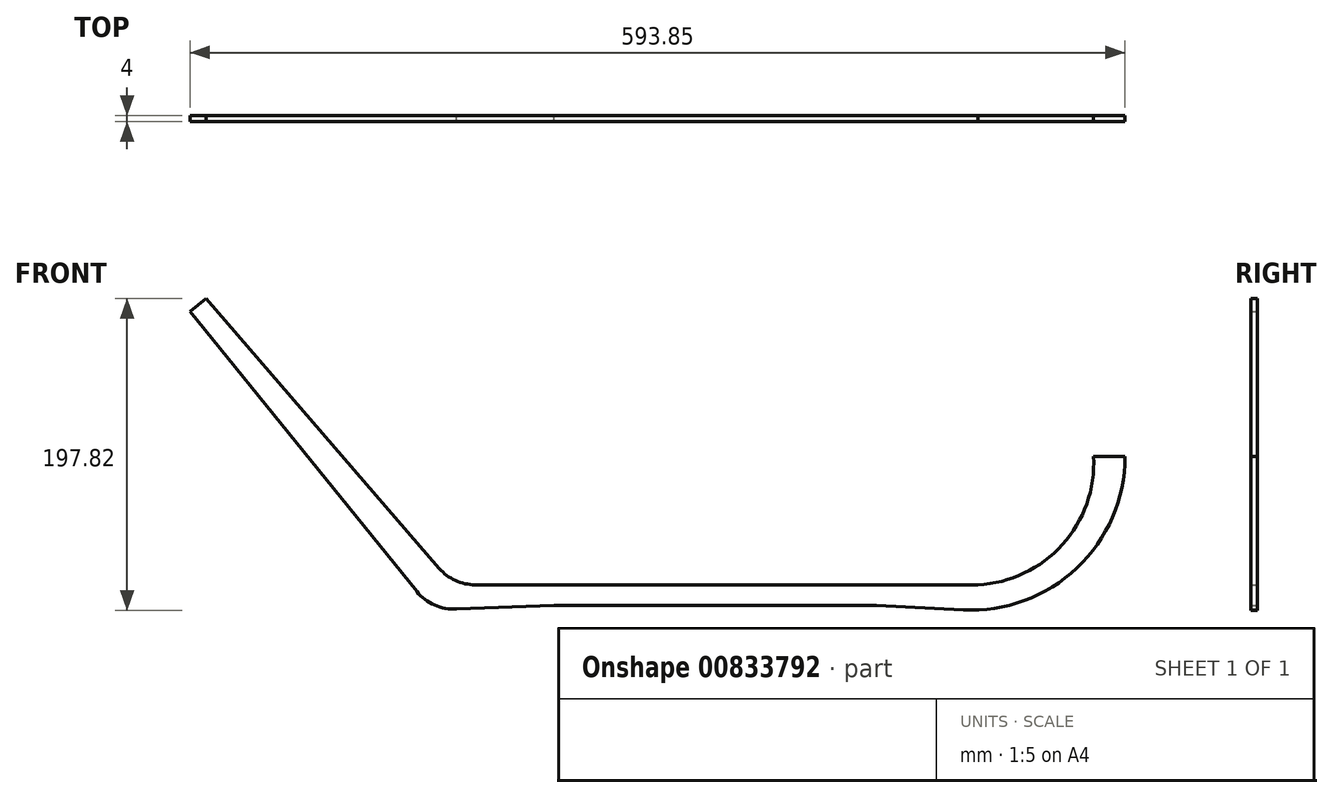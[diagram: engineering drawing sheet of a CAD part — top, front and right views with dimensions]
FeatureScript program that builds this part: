
annotation { "Feature Type Name" : "Feature", "Feature Type Description" : "" }
export const myFeature = defineFeature(function(context is Context, id is Id, definition is map)
    precondition{}
    {
        {
            var Q0;
            Q0=qCreatedBy(makeId("Front.planeOp"),FACE);
            var sketch = newSketch(context, id + "F0", { "sketchPlane" : qUnion([Q0])});
            skLineSegment(sketch, "E0", {"start": v(-241.53, -17.56) * mm, "end": v(-385.53, 160.27) * mm});
            skLineSegment(sketch, "E1.1", {"start": v(-204.57, -13.25) * mm, "end": v(114.87, -13.25) * mm});
            skLineSegment(sketch, "E2", {"start": v(-375.43, 168.45) * mm, "end": v(-385.53, 160.27) * mm});
            skLineSegment(sketch, "E3", {"start": v(-375.43, 168.45) * mm, "end": v(-227.26, -2.87) * mm});
            skLineSegment(sketch, "E4.trimOffspring", {"start": v(-154.47, -26.25) * mm, "end": v(40.51, -26.25) * mm});
            skArc(sketch, "E5.filletArc", {"start": v(-227.26, -2.87) * mm, "mid": v(-217.05, -10.53) * mm, "end": v(-204.57, -13.25) * mm});
            skArc(sketch, "E6.filletArc", {"start": v(-241.53, -17.56) * mm, "mid": v(-230.3, -26.13) * mm, "end": v(-216.4, -28.62) * mm});
            skLineSegment(sketch, "E7", {"start": v(50.5, -26.5) * mm, "end": v(105.5, -29.25) * mm});
            skArc(sketch, "E8", {"start": v(105.5, -29.25) * mm, "mid": v(177.74, -2.54) * mm, "end": v(208.32, 68.13) * mm});
            skArc(sketch, "E9.filletArc", {"start": v(50.5, -26.5) * mm, "mid": v(45.5, -26.3) * mm, "end": v(40.51, -26.25) * mm});
            skArc(sketch, "E10", {"start": v(114.87, -13.25) * mm, "mid": v(168.49, 12.25) * mm, "end": v(188.32, 68.2) * mm});
            skLineSegment(sketch, "E11", {"start": v(188.32, 68.2) * mm, "end": v(208.32, 68.13) * mm});
            skLineSegment(sketch, "E12", {"start": v(-154.47, -26.25) * mm, "end": v(-216.4, -28.62) * mm});
            skSolve(sketch);
        }
        {
            var Q0;
            Q0=makeQuery(id+"F0.imprint","IMPRINT",FACE,{"disambiguationData":[TD([[makeQuery(id+"F0.imprint","IMPRINT",EDGE,{"derivedFrom":sQuery(id+"F0.wireOp",EDGE,"E0")}),-1.0]])]});
            extrude(context, id + "F1", {"entities" : qUnion([Q0]), "depth" : 4 * mm, "offsetDistance" : 25 * mm});
        }
    });
